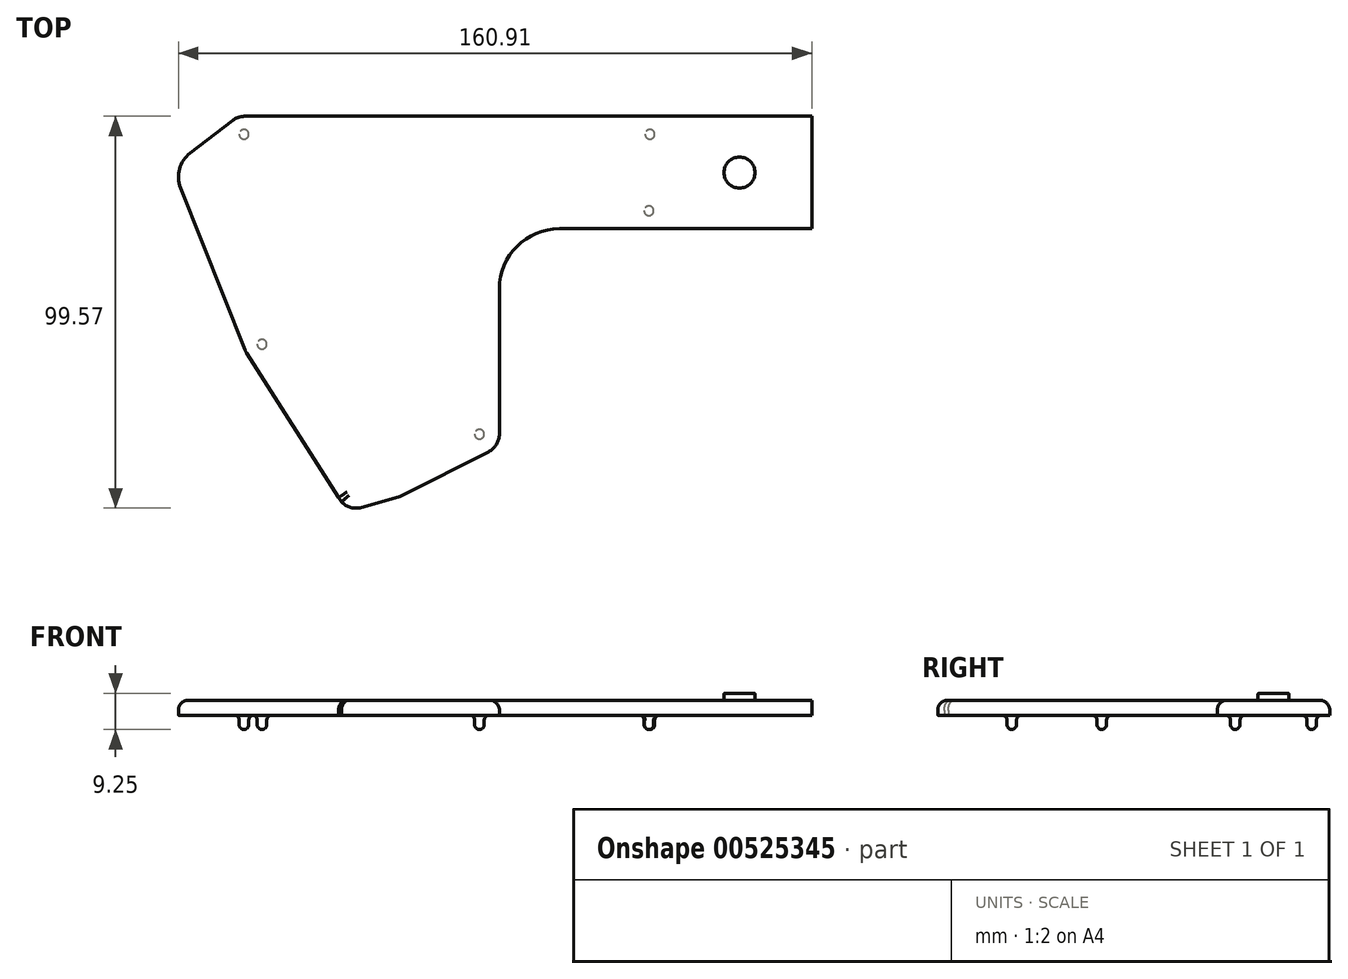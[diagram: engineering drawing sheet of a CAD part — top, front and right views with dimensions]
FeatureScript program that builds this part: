
annotation { "Feature Type Name" : "Feature", "Feature Type Description" : "" }
export const myFeature = defineFeature(function(context is Context, id is Id, definition is map)
    precondition{}
    {
        {
            var Q0;
            Q0=qCreatedBy(makeId("Top.planeOp"),FACE);
            var sketch = newSketch(context, id + "F0", { "sketchPlane" : qUnion([Q0])});
            skLineSegment(sketch, "E0.0", {"start": v(-43.43, -337.67) * mm, "end": v(-15.96, -337.67) * mm});
            skLineSegment(sketch, "E1.0", {"start": v(-160.03, -337.67) * mm, "end": v(-44.7, -337.67) * mm});
            skLineSegment(sketch, "E2.0", {"start": v(-43.43, -309.1) * mm, "end": v(-15.96, -309.1) * mm});
            skLineSegment(sketch, "E3.0", {"start": v(-80.1, -309.1) * mm, "end": v(-44.7, -309.1) * mm});
            skArc(sketch, "E4.0", {"start": v(-80.1, -309.1) * mm, "mid": v(-90.87, -304.63) * mm, "end": v(-95.34, -293.85) * mm});
            skLineSegment(sketch, "E5.0", {"start": v(-95.34, -293.85) * mm, "end": v(-95.34, -256.97) * mm});
            skArc(sketch, "E6.0", {"start": v(-95.34, -256.97) * mm, "mid": v(-96.09, -254.3) * mm, "end": v(-98.12, -252.43) * mm});
            skLineSegment(sketch, "E7.0", {"start": v(-98.12, -252.43) * mm, "end": v(-120.03, -241.33) * mm});
            skArc(sketch, "E8.0", {"start": v(-120.03, -241.33) * mm, "mid": v(-120.47, -241.13) * mm, "end": v(-120.93, -240.97) * mm});
            skLineSegment(sketch, "E9.0", {"start": v(-130.32, -238.3) * mm, "end": v(-120.93, -240.97) * mm});
            skArc(sketch, "E10.0", {"start": v(-130.32, -238.3) * mm, "mid": v(-133.1, -238.29) * mm, "end": v(-135.45, -239.74) * mm});
            skLineSegment(sketch, "E11.0", {"start": v(-136.2, -240.77) * mm, "end": v(-141.2, -248.63) * mm});
            skLineSegment(sketch, "E12.0", {"start": v(-151.3, -264.49) * mm, "end": v(-159.82, -277.9) * mm});
            skLineSegment(sketch, "E13.0", {"start": v(-159.82, -277.9) * mm, "end": v(-165.67, -292.62) * mm});
            skLineSegment(sketch, "E14.0", {"start": v(-172.6, -310.09) * mm, "end": v(-176.33, -319.47) * mm});
            skArc(sketch, "E15.0", {"start": v(-176.33, -319.47) * mm, "mid": v(-176.6, -324.3) * mm, "end": v(-173.9, -328.33) * mm});
            skPoint(sketch, "E16.0", {"position": v(-168.51, -332.47) * mm});
            skLineSegment(sketch, "E17.0", {"start": v(-173.9, -328.33) * mm, "end": v(-163.13, -336.61) * mm});
            skArc(sketch, "E18.0", {"start": v(-163.13, -336.61) * mm, "mid": v(-161.67, -337.4) * mm, "end": v(-160.03, -337.67) * mm});
            skLineSegment(sketch, "E19", {"start": v(-172.6, -310.09) * mm, "end": v(-165.67, -292.62) * mm});
            skLineSegment(sketch, "E20", {"start": v(-151.3, -264.49) * mm, "end": v(-141.2, -248.63) * mm});
            skLineSegment(sketch, "E21", {"start": v(-136.2, -240.77) * mm, "end": v(-135.45, -239.74) * mm});
            skLineSegment(sketch, "E22", {"start": v(-44.7, -309.1) * mm, "end": v(-43.43, -309.1) * mm});
            skLineSegment(sketch, "E23", {"start": v(-44.7, -337.67) * mm, "end": v(-43.43, -337.67) * mm});
            skLineSegment(sketch, "E24", {"start": v(-15.96, -337.67) * mm, "end": v(-15.96, -309.1) * mm});
            skSolve(sketch);
        }
        {
            var Q0;
            Q0=makeQuery(id+"F0.imprint","IMPRINT",FACE,{"disambiguationData":[TD([[makeQuery(id+"F0.imprint","IMPRINT",EDGE,{"derivedFrom":sQuery(id+"F0.wireOp",EDGE,"d1444f51-8acc-4532-b601-094db481933f.0")}),-1.0]])]});
            var Q1;
            Q1=makeQuery(id+"F0.imprint","IMPRINT",FACE,{"disambiguationData":[TD([[makeQuery(id+"F0.imprint","IMPRINT",EDGE,{"derivedFrom":sQuery(id+"F0.wireOp",EDGE,"E0.0")}),1.0]])]});
            var Q2;
            Q2=qConstructionFilter(qBodyType(qCreatedBy(id+"F0",EDGE),BodyType.WIRE),ConstructionObject.NO);
            extrude(context, id + "F1", {"entities" : qUnion([Q0, Q1]), "surfaceEntities" : qUnion([Q2]), "depth" : 3.81 * mm, "offsetDistance" : 25.4 * mm});
        }
        {
            var Q0;
            Q0=makeQuery(id+"F1.opExtrude","CAP_EDGE",EDGE,{"disambiguationData":[OSD([sQuery(id+"F0.wireOp",EDGE,"E21")])],"isStart":false});
            var Q1;
            Q1=makeQuery(id+"F1.opExtrude","CAP_EDGE",EDGE,{"disambiguationData":[OSD([sQuery(id+"F0.wireOp",EDGE,"E9.0")])],"isStart":false});
            var Q2;
            Q2=makeQuery(id+"F1.opExtrude","CAP_EDGE",EDGE,{"disambiguationData":[OSD([sQuery(id+"F0.wireOp",EDGE,"E0.0"),sQuery(id+"F0.wireOp",EDGE,"E1.0"),sQuery(id+"F0.wireOp",EDGE,"E23")])],"isStart":false});
            fillet(context, id + "F2", {"entities" : qUnion([Q0, Q1, Q2]), "radius" : 2.54 * mm, "tangentPropagation" : true, "allowEdgeOverflow" : false});
        }
        {
            var Q0;
            Q0=makeQuery(id+"F1.opExtrude","CAP_FACE",FACE,{"disambiguationData":[OSD([sQuery(id+"F0.wireOp",EDGE,"E0.0"),sQuery(id+"F0.wireOp",EDGE,"E1.0"),sQuery(id+"F0.wireOp",EDGE,"E2.0"),sQuery(id+"F0.wireOp",EDGE,"E3.0"),sQuery(id+"F0.wireOp",EDGE,"E4.0"),sQuery(id+"F0.wireOp",EDGE,"E5.0"),sQuery(id+"F0.wireOp",EDGE,"E6.0"),sQuery(id+"F0.wireOp",EDGE,"E7.0"),sQuery(id+"F0.wireOp",EDGE,"E8.0"),sQuery(id+"F0.wireOp",EDGE,"E9.0"),sQuery(id+"F0.wireOp",EDGE,"E10.0"),sQuery(id+"F0.wireOp",EDGE,"E11.0"),sQuery(id+"F0.wireOp",EDGE,"E12.0"),sQuery(id+"F0.wireOp",EDGE,"E13.0"),sQuery(id+"F0.wireOp",EDGE,"E14.0"),sQuery(id+"F0.wireOp",EDGE,"E15.0"),sQuery(id+"F0.wireOp",EDGE,"E17.0"),sQuery(id+"F0.wireOp",EDGE,"E18.0"),sQuery(id+"F0.wireOp",EDGE,"E19"),sQuery(id+"F0.wireOp",EDGE,"E20"),sQuery(id+"F0.wireOp",EDGE,"E21"),sQuery(id+"F0.wireOp",EDGE,"E22"),sQuery(id+"F0.wireOp",EDGE,"E23"),sQuery(id+"F0.wireOp",EDGE,"E24")])],"isStart":false});
            var sketch = newSketch(context, id + "F3", { "sketchPlane" : qUnion([Q0])});
            skCircle(sketch, "E25.0", {"center": v(-34.35, -323.38) * mm, "radius": 3.94 * mm});
            skLineSegment(sketch, "E26", {"start": v(-97.88, -323.38) * mm, "end": v(-34.35, -323.38) * mm});
            skLineSegment(sketch, "E27", {"start": v(-97.88, -293.85) * mm, "end": v(-97.88, -335.13) * mm});
            skLineSegment(sketch, "E28", {"start": v(-34.35, -323.38) * mm, "end": v(-34.35, -311.63) * mm});
            skLineSegment(sketch, "E29", {"start": v(-34.35, -323.38) * mm, "end": v(-34.35, -335.13) * mm});
            skSolve(sketch);
        }
        {
            var Q0;
            Q0=qSketchRegion(id+"F3",true);
            extrude(context, id + "F4", {"entities" : qUnion([Q0]), "operationType" : NewBodyOperationType.ADD, "depth" : 1.78 * mm});
        }
        {
            var Q0;
            Q0=makeQuery(id+"F1.opExtrude","SWEPT_EDGE",EDGE,{"disambiguationData":[OSD([sQuery(id+"F0.wireOp",EDGE,"E12.0"),sQuery(id+"F0.wireOp",EDGE,"E13.0")])]});
            fillet(context, id + "F5", {"entities" : qUnion([Q0]), "radius" : 5.08 * mm, "tangentPropagation" : true, "allowEdgeOverflow" : false});
        }
        {
            var Q0;
            Q0=makeQuery(id+"F1.opExtrude","CAP_FACE",FACE,{"disambiguationData":[OSD([sQuery(id+"F0.wireOp",EDGE,"E0.0"),sQuery(id+"F0.wireOp",EDGE,"E1.0"),sQuery(id+"F0.wireOp",EDGE,"E2.0"),sQuery(id+"F0.wireOp",EDGE,"E3.0"),sQuery(id+"F0.wireOp",EDGE,"E4.0"),sQuery(id+"F0.wireOp",EDGE,"E5.0"),sQuery(id+"F0.wireOp",EDGE,"E6.0"),sQuery(id+"F0.wireOp",EDGE,"E7.0"),sQuery(id+"F0.wireOp",EDGE,"E8.0"),sQuery(id+"F0.wireOp",EDGE,"E9.0"),sQuery(id+"F0.wireOp",EDGE,"E10.0"),sQuery(id+"F0.wireOp",EDGE,"E11.0"),sQuery(id+"F0.wireOp",EDGE,"E12.0"),sQuery(id+"F0.wireOp",EDGE,"E13.0"),sQuery(id+"F0.wireOp",EDGE,"E14.0"),sQuery(id+"F0.wireOp",EDGE,"E15.0"),sQuery(id+"F0.wireOp",EDGE,"E17.0"),sQuery(id+"F0.wireOp",EDGE,"E18.0"),sQuery(id+"F0.wireOp",EDGE,"E19"),sQuery(id+"F0.wireOp",EDGE,"E20"),sQuery(id+"F0.wireOp",EDGE,"E21"),sQuery(id+"F0.wireOp",EDGE,"E22"),sQuery(id+"F0.wireOp",EDGE,"E23"),sQuery(id+"F0.wireOp",EDGE,"E24")])],"isStart":true});
            var sketch = newSketch(context, id + "F6", { "sketchPlane" : qUnion([Q0])});
            skLineSegment(sketch, "E30", {"start": v(-57.11, 333.03) * mm, "end": v(-57.11, 337.67) * mm});
            skLineSegment(sketch, "E31", {"start": v(-125.27, 333.03) * mm, "end": v(-9.65, 333.03) * mm});
            skSolve(sketch);
        }
        {
            var Q0;
            Q0=makeQuery(id+"F1.opExtrude","SWEPT_FACE",FACE,{"disambiguationData":[OSD([sQuery(id+"F0.wireOp",EDGE,"E0.0"),sQuery(id+"F0.wireOp",EDGE,"E1.0"),sQuery(id+"F0.wireOp",EDGE,"E23")])]});
            cPlane(context, id + "F7", {"entities" : qUnion([Q0]), "cplaneType" : CPlaneType.OFFSET, "offset" : 4.57 * mm, "oppositeDirection" : true, "width" : 152.4 * mm, "height" : 152.4 * mm});
        }
        {
            var Q0;
            Q0=qCreatedBy(id+"F7.planeOp",FACE);
            var sketch = newSketch(context, id + "F8", { "sketchPlane" : qUnion([Q0])});
            skLineSegment(sketch, "E32.bottom", {"start": v(-58.33, -2.39) * mm, "end": v(-58.33, -1.27) * mm});
            skLineSegment(sketch, "E32.left", {"start": v(-37.58, -6.33) * mm, "end": v(-37.58, -6.33) * mm});
            skPoint(sketch, "E33.visualSharp", {"position": v(-36.99, -12.97) * mm});
            skPoint(sketch, "E34.visualSharp", {"position": v(-58.33, -12.97) * mm});
            skArc(sketch, "E34.filletArc", {"start": v(-58.33, -2.39) * mm, "mid": v(-57.96, -3.28) * mm, "end": v(-57.06, -3.66) * mm});
            skLineSegment(sketch, "E35", {"start": v(-59.6, 0) * mm, "end": v(-60.04, 0) * mm});
            skArc(sketch, "E36.filletArc", {"start": v(-58.33, -1.27) * mm, "mid": v(-58.7, -0.37) * mm, "end": v(-59.6, 0) * mm});
            skLineSegment(sketch, "E37", {"start": v(-60.04, 0) * mm, "end": v(-54.18, 0) * mm});
            skLineSegment(sketch, "E38", {"start": v(-58.33, -1.27) * mm, "end": v(-58.33, 0) * mm});
            skLineSegment(sketch, "E39", {"start": v(-57.11, -3.66) * mm, "end": v(-57.11, 0) * mm});
            skSolve(sketch);
        }
        {
            var Q0;
            {var subQ5=sQuery(id+"F8.wireOp",EDGE,"E32.bottom");Q0=makeQuery(id+"F8.imprint","IMPRINT",FACE,{"disambiguationData":[TD([[makeQuery(id+"F8.imprint","IMPRINT",EDGE,{"derivedFrom":subQ5}),-1.0]])]});}
            var Q1;
            {var subQ0=sQuery(id+"F8.wireOp",EDGE,"E36.filletArc");Q1=makeQuery(id+"F8.imprint","IMPRINT",FACE,{"disambiguationData":[TD([[makeQuery(id+"F8.imprint","IMPRINT",EDGE,{"derivedFrom":subQ0}),-1.0]])]});}
            var Q2;
            Q2=sQuery(id+"F8.wireOp",EDGE,"E32.bottom");
            var Q3;
            Q3=sQuery(id+"F8.wireOp",EDGE,"E34.filletArc");
            var Q4;
            Q4=sQuery(id+"F8.wireOp",EDGE,"E39");
            var Q5;
            Q5=sQuery(id+"F8.wireOp",EDGE,"E38");
            var Q6;
            Q6=sQuery(id+"F8.wireOp",EDGE,"E36.filletArc");
            var Q7;
            Q7=sQuery(id+"F8.wireOp",EDGE,"E35");
            var Q8;
            Q8=sQuery(id+"F8.wireOp",EDGE,"E37");
            var Q9;
            Q9=sQuery(id+"F8.wireOp",EDGE,"E39");
            revolve(context, id + "F9", {"operationType" : NewBodyOperationType.ADD, "entities" : qUnion([Q0, Q1]), "surfaceEntities" : qUnion([Q2, Q3, Q4, Q5, Q6, Q7, Q8]), "axis" : qUnion([Q9]), "revolveType" : RevolveType.FULL});
        }
        {
            var Q0;
            {var subQ6=sQuery(id+"F6.wireOp",EDGE,"E30");Q0=makeQuery(id+"F6.imprint","IMPRINT",FACE,{"disambiguationData":[TD([[makeQuery(id+"F6.imprint","IMPRINT",EDGE,{"derivedFrom":subQ6}),1.0]])]});}
            var sketch = newSketch(context, id + "F10", { "sketchPlane" : qUnion([Q0])});
            skLineSegment(sketch, "E40", {"start": v(-15.96, 313.66) * mm, "end": v(-57.36, 313.66) * mm});
            skLineSegment(sketch, "E41", {"start": v(-57.36, 309.1) * mm, "end": v(-57.36, 313.66) * mm});
            skLineSegment(sketch, "E42.0", {"start": v(-80.1, 309.1) * mm, "end": v(-15.96, 309.1) * mm});
            skLineSegment(sketch, "E43.0", {"start": v(-15.96, 337.67) * mm, "end": v(-15.96, 309.1) * mm});
            skSolve(sketch);
        }
        {
            var Q0;
            Q0=makeQuery(id+"F1.opExtrude","SWEPT_FACE",FACE,{"disambiguationData":[OSD([sQuery(id+"F0.wireOp",EDGE,"E2.0"),sQuery(id+"F0.wireOp",EDGE,"E3.0"),sQuery(id+"F0.wireOp",EDGE,"E22")])]});
            cPlane(context, id + "F11", {"entities" : qUnion([Q0]), "cplaneType" : CPlaneType.OFFSET, "offset" : 4.57 * mm, "oppositeDirection" : true, "width" : 152.4 * mm, "height" : 152.4 * mm});
        }
        {
            var Q0;
            Q0=qCreatedBy(id+"F11.planeOp",FACE);
            var sketch = newSketch(context, id + "F12", { "sketchPlane" : qUnion([Q0])});
            skLineSegment(sketch, "E44.bottom", {"start": v(56.15, -2.39) * mm, "end": v(56.15, -1.27) * mm});
            skArc(sketch, "E45.filletArc", {"start": v(56.15, -2.39) * mm, "mid": v(56.52, -3.28) * mm, "end": v(57.42, -3.66) * mm});
            skLineSegment(sketch, "E46", {"start": v(54.88, 0) * mm, "end": v(54.43, 0) * mm});
            skArc(sketch, "E47.filletArc", {"start": v(56.15, -1.27) * mm, "mid": v(55.77, -0.37) * mm, "end": v(54.88, 0) * mm});
            skLineSegment(sketch, "E48", {"start": v(54.43, 0) * mm, "end": v(60.3, 0) * mm});
            skLineSegment(sketch, "E49", {"start": v(56.15, -1.27) * mm, "end": v(56.15, 0) * mm});
            skLineSegment(sketch, "E50", {"start": v(57.36, -3.66) * mm, "end": v(57.36, 0) * mm});
            skSolve(sketch);
        }
        {
            var Q0;
            Q0=qSketchRegion(id+"F12",true);
            var Q1;
            Q1=sQuery(id+"F12.wireOp",EDGE,"E50");
            revolve(context, id + "F13", {"operationType" : NewBodyOperationType.ADD, "entities" : qUnion([Q0]), "axis" : qUnion([Q1]), "revolveType" : RevolveType.FULL});
        }
        {
            var Q0;
            {var subQ6=sQuery(id+"F6.wireOp",EDGE,"E30");Q0=makeQuery(id+"F6.imprint","IMPRINT",FACE,{"disambiguationData":[TD([[makeQuery(id+"F6.imprint","IMPRINT",EDGE,{"derivedFrom":subQ6}),1.0]])]});}
            var sketch = newSketch(context, id + "F14", { "sketchPlane" : qUnion([Q0])});
            skLineSegment(sketch, "E51", {"start": v(-100.42, 256.9) * mm, "end": v(-100.42, 363.43) * mm});
            skLineSegment(sketch, "E52", {"start": v(-95.34, 256.9) * mm, "end": v(-100.42, 256.9) * mm});
            skLineSegment(sketch, "E53.0", {"start": v(-95.34, 293.85) * mm, "end": v(-95.34, 256.97) * mm});
            skArc(sketch, "E54.0", {"start": v(-95.34, 256.97) * mm, "mid": v(-96.09, 254.3) * mm, "end": v(-98.12, 252.43) * mm});
            skSolve(sketch);
        }
        {
            var Q0;
            Q0=makeQuery(id+"F1.opExtrude","SWEPT_FACE",FACE,{"disambiguationData":[OSD([sQuery(id+"F0.wireOp",EDGE,"E0.0"),sQuery(id+"F0.wireOp",EDGE,"E1.0"),sQuery(id+"F0.wireOp",EDGE,"E23")])]});
            cPlane(context, id + "F15", {"entities" : qUnion([Q0]), "cplaneType" : CPlaneType.OFFSET, "offset" : 80.77 * mm, "oppositeDirection" : true, "width" : 152.4 * mm, "height" : 152.4 * mm});
        }
        {
            var Q0;
            Q0=qCreatedBy(id+"F15.planeOp",FACE);
            var sketch = newSketch(context, id + "F16", { "sketchPlane" : qUnion([Q0])});
            skLineSegment(sketch, "E55.bottom", {"start": v(-101.64, -2.39) * mm, "end": v(-101.64, -1.27) * mm});
            skArc(sketch, "E56.filletArc", {"start": v(-101.64, -2.39) * mm, "mid": v(-101.27, -3.28) * mm, "end": v(-100.37, -3.66) * mm});
            skLineSegment(sketch, "E57", {"start": v(-102.9, 0) * mm, "end": v(-103.35, 0) * mm});
            skArc(sketch, "E58.filletArc", {"start": v(-101.64, -1.27) * mm, "mid": v(-102, -0.37) * mm, "end": v(-102.9, 0) * mm});
            skLineSegment(sketch, "E59", {"start": v(-103.35, 0) * mm, "end": v(-97.48, 0) * mm});
            skLineSegment(sketch, "E60", {"start": v(-101.64, -1.27) * mm, "end": v(-101.64, 0) * mm});
            skLineSegment(sketch, "E61", {"start": v(-100.42, -3.66) * mm, "end": v(-100.42, 0) * mm});
            skSolve(sketch);
        }
        {
            var Q0;
            Q0=qSketchRegion(id+"F16",true);
            var Q1;
            Q1=sQuery(id+"F16.wireOp",EDGE,"E61");
            revolve(context, id + "F17", {"operationType" : NewBodyOperationType.ADD, "entities" : qUnion([Q0]), "axis" : qUnion([Q1]), "revolveType" : RevolveType.FULL});
        }
        {
            var Q0;
            {var subQ6=sQuery(id+"F6.wireOp",EDGE,"E30");Q0=makeQuery(id+"F6.imprint","IMPRINT",FACE,{"disambiguationData":[TD([[makeQuery(id+"F6.imprint","IMPRINT",EDGE,{"derivedFrom":subQ6}),1.0]])]});}
            var sketch = newSketch(context, id + "F18", { "sketchPlane" : qUnion([Q0])});
            skLineSegment(sketch, "E62", {"start": v(-160.23, 333.1) * mm, "end": v(-160.23, 337.66) * mm});
            skLineSegment(sketch, "E63", {"start": v(-100.12, 333.1) * mm, "end": v(-163.57, 333.1) * mm});
            skSolve(sketch);
        }
        {
            var Q0;
            Q0=qCreatedBy(id+"F7.planeOp",FACE);
            var sketch = newSketch(context, id + "F19", { "sketchPlane" : qUnion([Q0])});
            skLineSegment(sketch, "E64.bottom", {"start": v(-161.45, -2.39) * mm, "end": v(-161.45, -1.27) * mm});
            skArc(sketch, "E65.filletArc", {"start": v(-161.45, -2.39) * mm, "mid": v(-161.08, -3.28) * mm, "end": v(-160.18, -3.66) * mm});
            skLineSegment(sketch, "E66", {"start": v(-162.72, 0) * mm, "end": v(-163.17, 0) * mm});
            skArc(sketch, "E67.filletArc", {"start": v(-161.45, -1.27) * mm, "mid": v(-161.83, -0.37) * mm, "end": v(-162.72, 0) * mm});
            skLineSegment(sketch, "E68", {"start": v(-163.17, 0) * mm, "end": v(-157.3, 0) * mm});
            skLineSegment(sketch, "E69", {"start": v(-161.45, -1.27) * mm, "end": v(-161.45, 0) * mm});
            skLineSegment(sketch, "E70", {"start": v(-160.23, -3.66) * mm, "end": v(-160.23, 0) * mm});
            skSolve(sketch);
        }
        {
            var Q0;
            Q0=qSketchRegion(id+"F19",true);
            var Q1;
            Q1=sQuery(id+"F19.wireOp",EDGE,"E70");
            revolve(context, id + "F20", {"operationType" : NewBodyOperationType.ADD, "entities" : qUnion([Q0]), "axis" : qUnion([Q1]), "revolveType" : RevolveType.FULL});
        }
        {
            var Q0;
            {var subQ6=sQuery(id+"F6.wireOp",EDGE,"E30");Q0=makeQuery(id+"F6.imprint","IMPRINT",FACE,{"disambiguationData":[TD([[makeQuery(id+"F6.imprint","IMPRINT",EDGE,{"derivedFrom":subQ6}),1.0]])]});}
            var sketch = newSketch(context, id + "F21", { "sketchPlane" : qUnion([Q0])});
            skLineSegment(sketch, "E71", {"start": v(-155.66, 279.75) * mm, "end": v(-155.66, 448.27) * mm});
            skLineSegment(sketch, "E72", {"start": v(-46.55, 279.75) * mm, "end": v(-228.58, 279.75) * mm});
            skLineSegment(sketch, "E73.0", {"start": v(-136.2, 240.77) * mm, "end": v(-159.56, 277.49) * mm});
            skLineSegment(sketch, "E74.0", {"start": v(-176.33, 319.47) * mm, "end": v(-160, 278.34) * mm});
            skArc(sketch, "E75.0", {"start": v(-160, 278.34) * mm, "mid": v(-159.8, 277.9) * mm, "end": v(-159.56, 277.49) * mm});
            skSolve(sketch);
        }
        {
            var Q0;
            Q0=makeQuery(id+"F1.opExtrude","SWEPT_FACE",FACE,{"disambiguationData":[OSD([sQuery(id+"F0.wireOp",EDGE,"E0.0"),sQuery(id+"F0.wireOp",EDGE,"E1.0"),sQuery(id+"F0.wireOp",EDGE,"E23")])]});
            cPlane(context, id + "F22", {"entities" : qUnion([Q0]), "cplaneType" : CPlaneType.OFFSET, "offset" : 57.9 * mm, "oppositeDirection" : true, "width" : 152.4 * mm, "height" : 152.4 * mm});
        }
        {
            var Q0;
            Q0=qCreatedBy(id+"F22.planeOp",FACE);
            var sketch = newSketch(context, id + "F23", { "sketchPlane" : qUnion([Q0])});
            skLineSegment(sketch, "E76.bottom", {"start": v(-156.88, -2.39) * mm, "end": v(-156.88, -1.27) * mm});
            skArc(sketch, "E77.filletArc", {"start": v(-156.88, -2.39) * mm, "mid": v(-156.51, -3.28) * mm, "end": v(-155.61, -3.66) * mm});
            skLineSegment(sketch, "E78", {"start": v(-158.15, 0) * mm, "end": v(-158.6, 0) * mm});
            skArc(sketch, "E79.filletArc", {"start": v(-156.88, -1.27) * mm, "mid": v(-157.25, -0.37) * mm, "end": v(-158.15, 0) * mm});
            skLineSegment(sketch, "E80", {"start": v(-158.6, 0) * mm, "end": v(-152.73, 0) * mm});
            skLineSegment(sketch, "E81", {"start": v(-156.88, -1.27) * mm, "end": v(-156.88, 0) * mm});
            skLineSegment(sketch, "E82", {"start": v(-155.66, -3.66) * mm, "end": v(-155.66, 0) * mm});
            skSolve(sketch);
        }
        {
            var Q0;
            Q0=qSketchRegion(id+"F23",true);
            var Q1;
            Q1=sQuery(id+"F23.wireOp",EDGE,"E82");
            revolve(context, id + "F24", {"operationType" : NewBodyOperationType.ADD, "entities" : qUnion([Q0]), "axis" : qUnion([Q1]), "revolveType" : RevolveType.FULL});
        }
        {
            var Q0;
            Q0=makeQuery(id+"F4.opExtrude","CAP_EDGE",EDGE,{"disambiguationData":[OSD([sQuery(id+"F3.wireOp",EDGE,"E25.0")])],"isStart":false});
            fillet(context, id + "F25", {"entities" : qUnion([Q0]), "radius" : 0.25 * mm, "tangentPropagation" : true, "allowEdgeOverflow" : false});
        }
        {
            var Q0;
            Q0=makeQuery(id+"F1.opExtrude","SWEPT_BODY",BODY,{"disambiguationData":[OSD([sQuery(id+"F0.wireOp",EDGE,"E0.0"),sQuery(id+"F0.wireOp",EDGE,"E1.0"),sQuery(id+"F0.wireOp",EDGE,"E2.0"),sQuery(id+"F0.wireOp",EDGE,"E3.0"),sQuery(id+"F0.wireOp",EDGE,"E4.0"),sQuery(id+"F0.wireOp",EDGE,"E5.0"),sQuery(id+"F0.wireOp",EDGE,"E6.0"),sQuery(id+"F0.wireOp",EDGE,"E7.0"),sQuery(id+"F0.wireOp",EDGE,"E8.0"),sQuery(id+"F0.wireOp",EDGE,"E9.0"),sQuery(id+"F0.wireOp",EDGE,"E10.0"),sQuery(id+"F0.wireOp",EDGE,"E11.0"),sQuery(id+"F0.wireOp",EDGE,"E12.0"),sQuery(id+"F0.wireOp",EDGE,"E13.0"),sQuery(id+"F0.wireOp",EDGE,"E14.0"),sQuery(id+"F0.wireOp",EDGE,"E15.0"),sQuery(id+"F0.wireOp",EDGE,"E17.0"),sQuery(id+"F0.wireOp",EDGE,"E18.0"),sQuery(id+"F0.wireOp",EDGE,"E19"),sQuery(id+"F0.wireOp",EDGE,"E20"),sQuery(id+"F0.wireOp",EDGE,"E21"),sQuery(id+"F0.wireOp",EDGE,"E22"),sQuery(id+"F0.wireOp",EDGE,"E23"),sQuery(id+"F0.wireOp",EDGE,"E24")])]});
            var Q1;
            Q1=qCreatedBy(makeId("Front.planeOp"),FACE);
            mirror(context, id + "F26", {"entities" : qUnion([Q0]), "mirrorPlane" : qUnion([Q1])});
        }
        {
            var Q0;
            Q0=makeQuery(id+"F1.opExtrude","SWEPT_BODY",BODY,{"disambiguationData":[OSD([sQuery(id+"F0.wireOp",EDGE,"E0.0"),sQuery(id+"F0.wireOp",EDGE,"E1.0"),sQuery(id+"F0.wireOp",EDGE,"E2.0"),sQuery(id+"F0.wireOp",EDGE,"E3.0"),sQuery(id+"F0.wireOp",EDGE,"E4.0"),sQuery(id+"F0.wireOp",EDGE,"E5.0"),sQuery(id+"F0.wireOp",EDGE,"E6.0"),sQuery(id+"F0.wireOp",EDGE,"E7.0"),sQuery(id+"F0.wireOp",EDGE,"E8.0"),sQuery(id+"F0.wireOp",EDGE,"E9.0"),sQuery(id+"F0.wireOp",EDGE,"E10.0"),sQuery(id+"F0.wireOp",EDGE,"E11.0"),sQuery(id+"F0.wireOp",EDGE,"E12.0"),sQuery(id+"F0.wireOp",EDGE,"E13.0"),sQuery(id+"F0.wireOp",EDGE,"E14.0"),sQuery(id+"F0.wireOp",EDGE,"E15.0"),sQuery(id+"F0.wireOp",EDGE,"E17.0"),sQuery(id+"F0.wireOp",EDGE,"E18.0"),sQuery(id+"F0.wireOp",EDGE,"E19"),sQuery(id+"F0.wireOp",EDGE,"E20"),sQuery(id+"F0.wireOp",EDGE,"E21"),sQuery(id+"F0.wireOp",EDGE,"E22"),sQuery(id+"F0.wireOp",EDGE,"E23"),sQuery(id+"F0.wireOp",EDGE,"E24")])]});
            deleteBodies(context, id + "F27", {"entities" : qUnion([Q0])});
        }
    });
